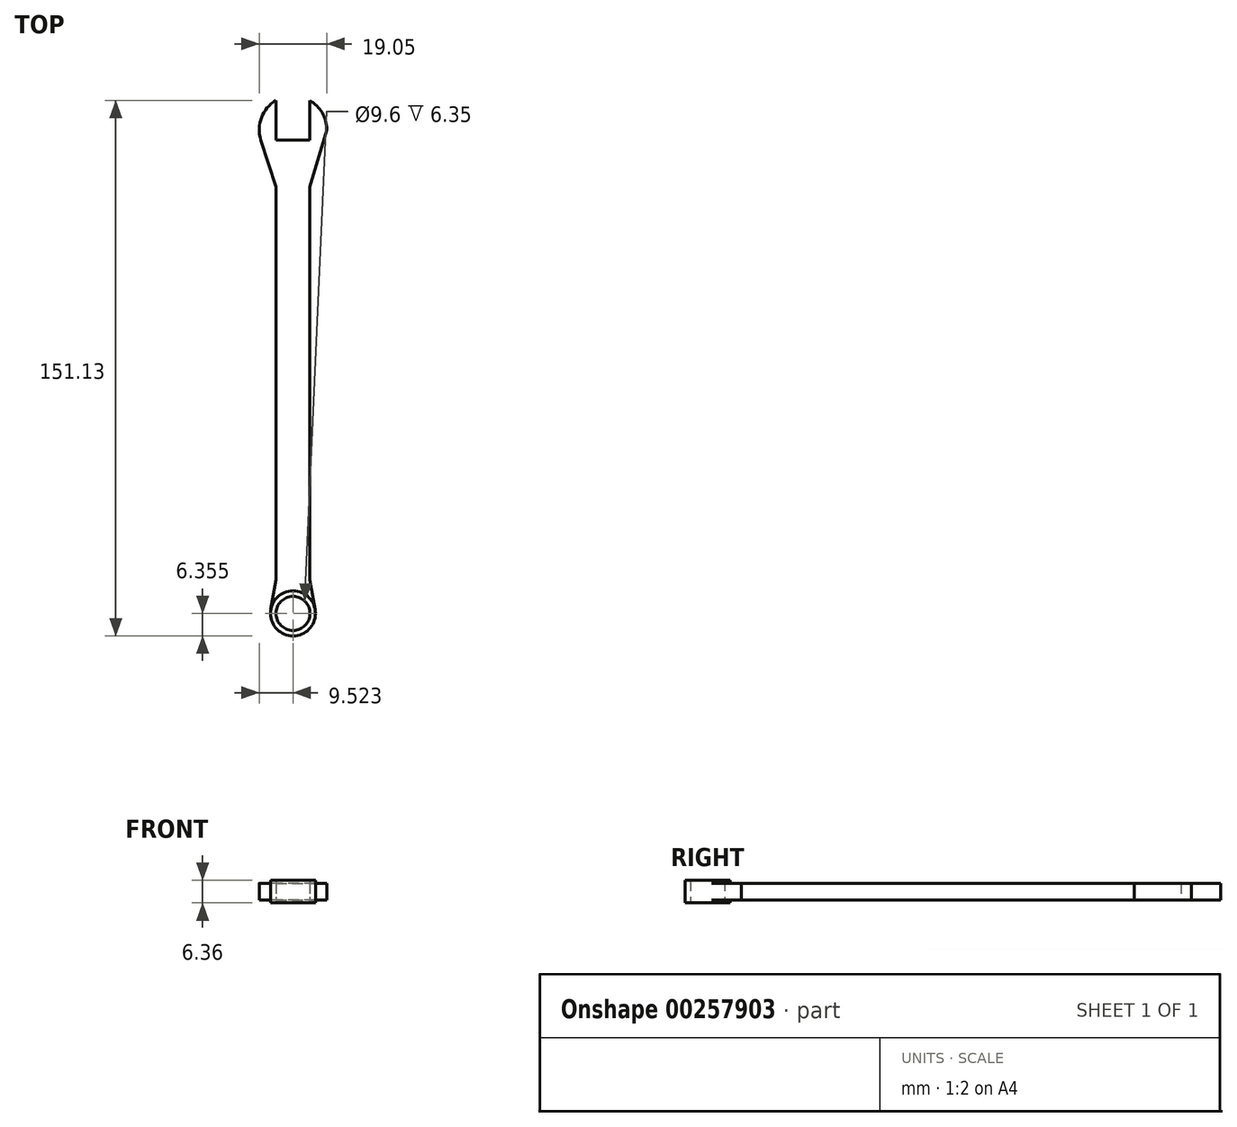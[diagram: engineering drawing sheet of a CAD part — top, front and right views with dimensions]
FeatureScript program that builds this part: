
annotation { "Feature Type Name" : "Feature", "Feature Type Description" : "" }
export const myFeature = defineFeature(function(context is Context, id is Id, definition is map)
    precondition{}
    {
        {
            var Q0;
            Q0=qCreatedBy(makeId("Top.planeOp"),FACE);
            var sketch = newSketch(context, id + "F0", { "sketchPlane" : qUnion([Q0])});
            skLineSegment(sketch, "E0", {"start": v(0, 0) * mm, "end": v(0, 110.86) * mm});
            skLineSegment(sketch, "E1", {"start": v(9.53, 110.86) * mm, "end": v(9.53, 0) * mm});
            skArc(sketch, "E2", {"start": v(12.76, 121.83) * mm, "mid": v(14.02, 129.23) * mm, "end": v(9.53, 135.25) * mm});
            skLineSegment(sketch, "E3", {"start": v(0, 110.86) * mm, "end": v(-4.3, 124.05) * mm});
            skLineSegment(sketch, "E4", {"start": v(9.52, 110.86) * mm, "end": v(14.29, 127) * mm});
            skPoint(sketch, "E5.orphan", {"position": v(0, 127) * mm});
            skPoint(sketch, "E6.end.orphan", {"position": v(9.53, 127) * mm});
            skLineSegment(sketch, "E7", {"start": v(0, 124.05) * mm, "end": v(9.52, 124.05) * mm});
            skLineSegment(sketch, "E8", {"start": v(0, 124.05) * mm, "end": v(0, 135.25) * mm});
            skLineSegment(sketch, "E9", {"start": v(9.52, 124.05) * mm, "end": v(9.52, 135.25) * mm});
            skArc(sketch, "E10.trimOffspring", {"start": v(0, 135.25) * mm, "mid": v(-4.13, 130.41) * mm, "end": v(-4.3, 124.05) * mm});
            skLineSegment(sketch, "E11.trimOffspring", {"start": v(13.42, 124.05) * mm, "end": v(13.82, 124.05) * mm});
            skCircle(sketch, "E12", {"center": v(4.76, -9.53) * mm, "radius": 6.35 * mm});
            skLineSegment(sketch, "E13", {"start": v(9.53, 0) * mm, "end": v(11.02, -8.42) * mm});
            skLineSegment(sketch, "E14", {"start": v(0, 0) * mm, "end": v(-1.5, -8.42) * mm});
            skPoint(sketch, "E15.orphan", {"position": v(4.76, 0) * mm});
            skCircle(sketch, "E16", {"center": v(4.76, -9.53) * mm, "radius": 4.8 * mm});
            skSolve(sketch);
        }
        {
            var Q0;
            Q0=makeQuery(id+"F0.imprint","IMPRINT",FACE,{"disambiguationData":[TD([[makeQuery(id+"F0.imprint","IMPRINT",EDGE,{"derivedFrom":sQuery(id+"F0.wireOp",EDGE,"E0")}),-1.0]])]});
            extrude(context, id + "F1", {"entities" : qUnion([Q0]), "endBound" : BoundingType.SYMMETRIC, "depth" : 3.17 * mm});
        }
        {
            var Q0;
            Q0=makeQuery(id+"F0.imprint","IMPRINT",FACE,{"disambiguationData":[TD([[makeQuery(id+"F0.imprint","IMPRINT",EDGE,{"derivedFrom":sQuery(id+"F0.wireOp",EDGE,"E3")}),-1.0]])]});
            extrude(context, id + "F2", {"entities" : qUnion([Q0]), "operationType" : NewBodyOperationType.ADD, "endBound" : BoundingType.SYMMETRIC, "depth" : 4.76 * mm});
        }
        {
            var Q0;
            Q0=makeQuery(id+"F0.imprint","IMPRINT",FACE,{"disambiguationData":[TD([[makeQuery(id+"F0.imprint","IMPRINT",EDGE,{"derivedFrom":sQuery(id+"F0.wireOp",EDGE,"E16")}),-1.0]])]});
            extrude(context, id + "F3", {"entities" : qUnion([Q0]), "operationType" : NewBodyOperationType.ADD, "endBound" : BoundingType.SYMMETRIC, "depth" : 6.35 * mm});
        }
    });
